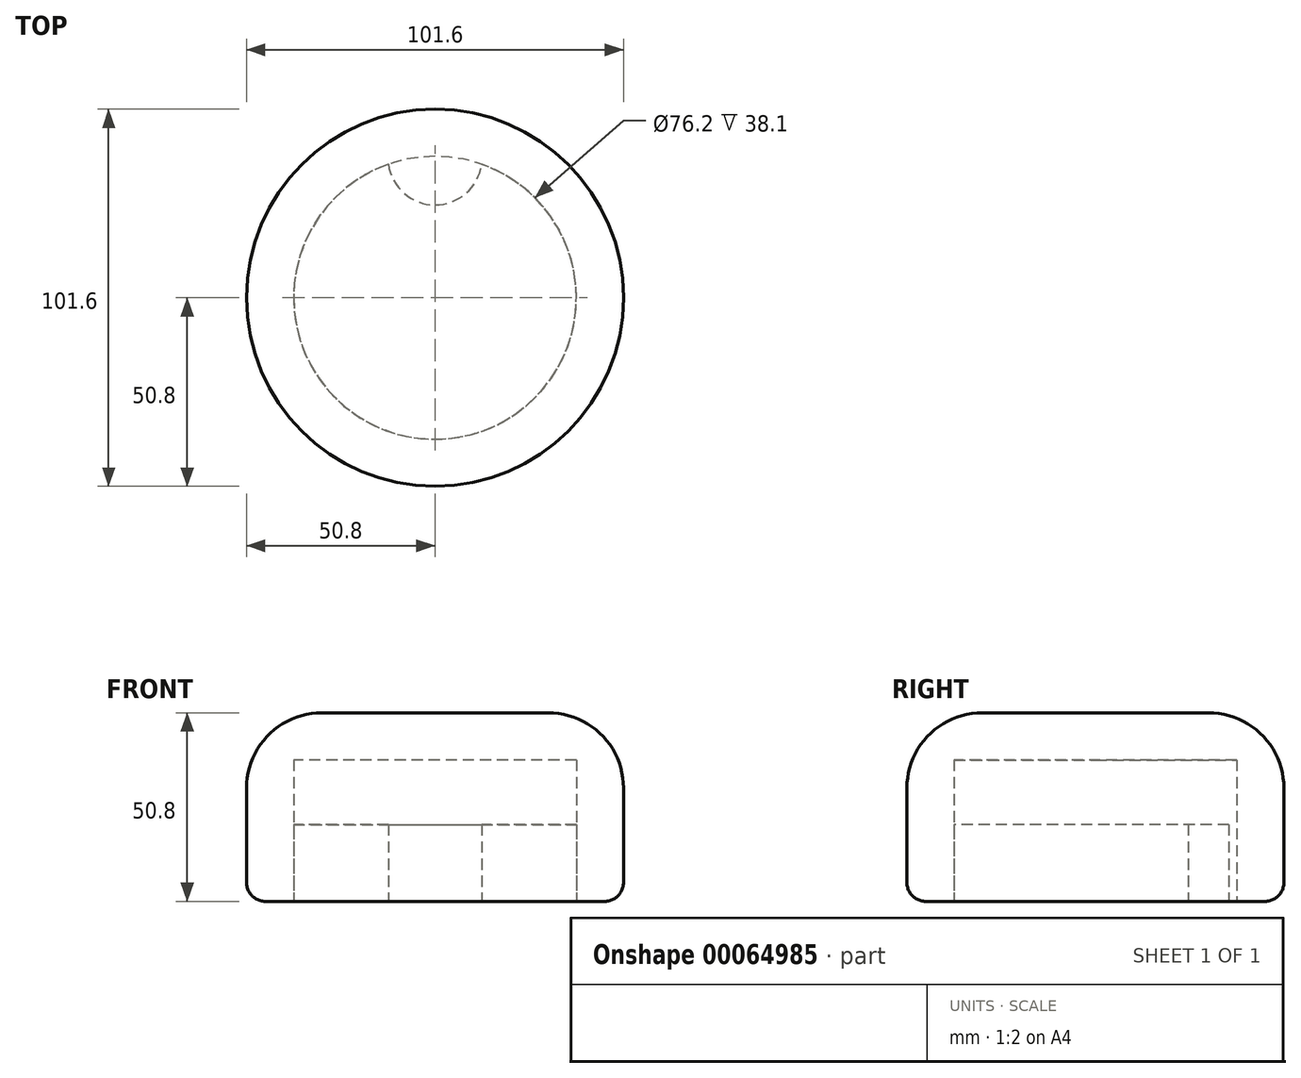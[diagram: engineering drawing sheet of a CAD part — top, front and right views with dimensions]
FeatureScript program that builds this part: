
annotation { "Feature Type Name" : "Feature", "Feature Type Description" : "" }
export const myFeature = defineFeature(function(context is Context, id is Id, definition is map)
    precondition{}
    {
        {
            var Q0;
            Q0=qCreatedBy(makeId("Top.planeOp"),FACE);
            var sketch = newSketch(context, id + "F0", { "sketchPlane" : qUnion([Q0])});
            skCircle(sketch, "E0", {"center": v(0, 0) * mm, "radius": 50.8 * mm});
            skCircle(sketch, "E1", {"center": v(0, 0) * mm, "radius": 38.1 * mm});
            skSolve(sketch);
        }
        {
            var Q0;
            Q0=makeQuery(id+"F0.imprint","IMPRINT",FACE,{"disambiguationData":[TD([[makeQuery(id+"F0.imprint","IMPRINT",EDGE,{"derivedFrom":sQuery(id+"F0.wireOp",EDGE,"E1")}),1.0]])]});
            var Q1;
            Q1=makeQuery(id+"F0.imprint","IMPRINT",FACE,{"disambiguationData":[TD([[makeQuery(id+"F0.imprint","IMPRINT",EDGE,{"derivedFrom":sQuery(id+"F0.wireOp",EDGE,"E0")}),1.0]])]});
            extrude(context, id + "F1", {"entities" : qUnion([Q0, Q1]), "depth" : 50.8 * mm});
        }
        {
            var Q0;
            Q0=makeQuery(id+"F0.imprint","IMPRINT",FACE,{"disambiguationData":[TD([[makeQuery(id+"F0.imprint","IMPRINT",EDGE,{"derivedFrom":sQuery(id+"F0.wireOp",EDGE,"E1")}),1.0]])]});
            extrude(context, id + "F2", {"entities" : qUnion([Q0]), "operationType" : NewBodyOperationType.REMOVE, "depth" : 38.1 * mm});
        }
        {
            var Q0;
            Q0=makeQuery(id+"F1.opExtrude","CAP_EDGE",EDGE,{"disambiguationData":[OSD([sQuery(id+"F0.wireOp",EDGE,"E0")])],"isStart":true});
            var Q1;
            Q1=makeQuery(id+"F2.boolean.opBoolean","COPY",EDGE,{"derivedFrom":makeQuery(id+"F2.opExtrude","CAP_EDGE",EDGE,{"disambiguationData":[OSD([sQuery(id+"F0.wireOp",EDGE,"E1")])],"isStart":true})});
            fillet(context, id + "F3", {"entities" : qUnion([Q0, Q1]), "radius" : 5.08 * mm, "tangentPropagation" : true, "allowEdgeOverflow" : false});
        }
        {
            var Q0;
            Q0=makeQuery(id+"F1.opExtrude","CAP_EDGE",EDGE,{"disambiguationData":[OSD([sQuery(id+"F0.wireOp",EDGE,"E0")])],"isStart":false});
            fillet(context, id + "F4", {"entities" : qUnion([Q0]), "radius" : 20.26 * mm, "tangentPropagation" : true, "allowEdgeOverflow" : false});
        }
        {
            var Q0;
            Q0=makeQuery(id+"F0.imprint","IMPRINT",FACE,{"disambiguationData":[TD([[makeQuery(id+"F0.imprint","IMPRINT",EDGE,{"derivedFrom":sQuery(id+"F0.wireOp",EDGE,"E1")}),1.0]])]});
            extrude(context, id + "F5", {"entities" : qUnion([Q0]), "depth" : 20.71 * mm});
        }
        {
            var Q0;
            Q0=makeQuery(id+"F0.imprint","IMPRINT",FACE,{"disambiguationData":[TD([[makeQuery(id+"F0.imprint","IMPRINT",EDGE,{"derivedFrom":sQuery(id+"F0.wireOp",EDGE,"E1")}),1.0]])]});
            var sketch = newSketch(context, id + "F6", { "sketchPlane" : qUnion([Q0])});
            skArc(sketch, "E2", {"start": v(-12.58, 35.96) * mm, "mid": v(0, 25.03) * mm, "end": v(12.58, 35.96) * mm});
            skCircle(sketch, "E3.0", {"center": v(0, 0) * mm, "radius": 38.1 * mm});
            skArc(sketch, "E4", {"start": v(12.58, 35.96) * mm, "mid": v(0, 38.1) * mm, "end": v(-12.58, 35.96) * mm});
            skSolve(sketch);
        }
        {
            var Q0;
            {var subQ0=sQuery(id+"F6.wireOp",EDGE,"E2");Q0=makeQuery(id+"F6.imprint","IMPRINT",FACE,{"disambiguationData":[TD([[makeQuery(id+"F6.imprint","IMPRINT",EDGE,{"derivedFrom":subQ0}),1.0]])]});}
            extrude(context, id + "F7", {"entities" : qUnion([Q0]), "operationType" : NewBodyOperationType.REMOVE, "depth" : 34.26 * mm});
        }
    });
